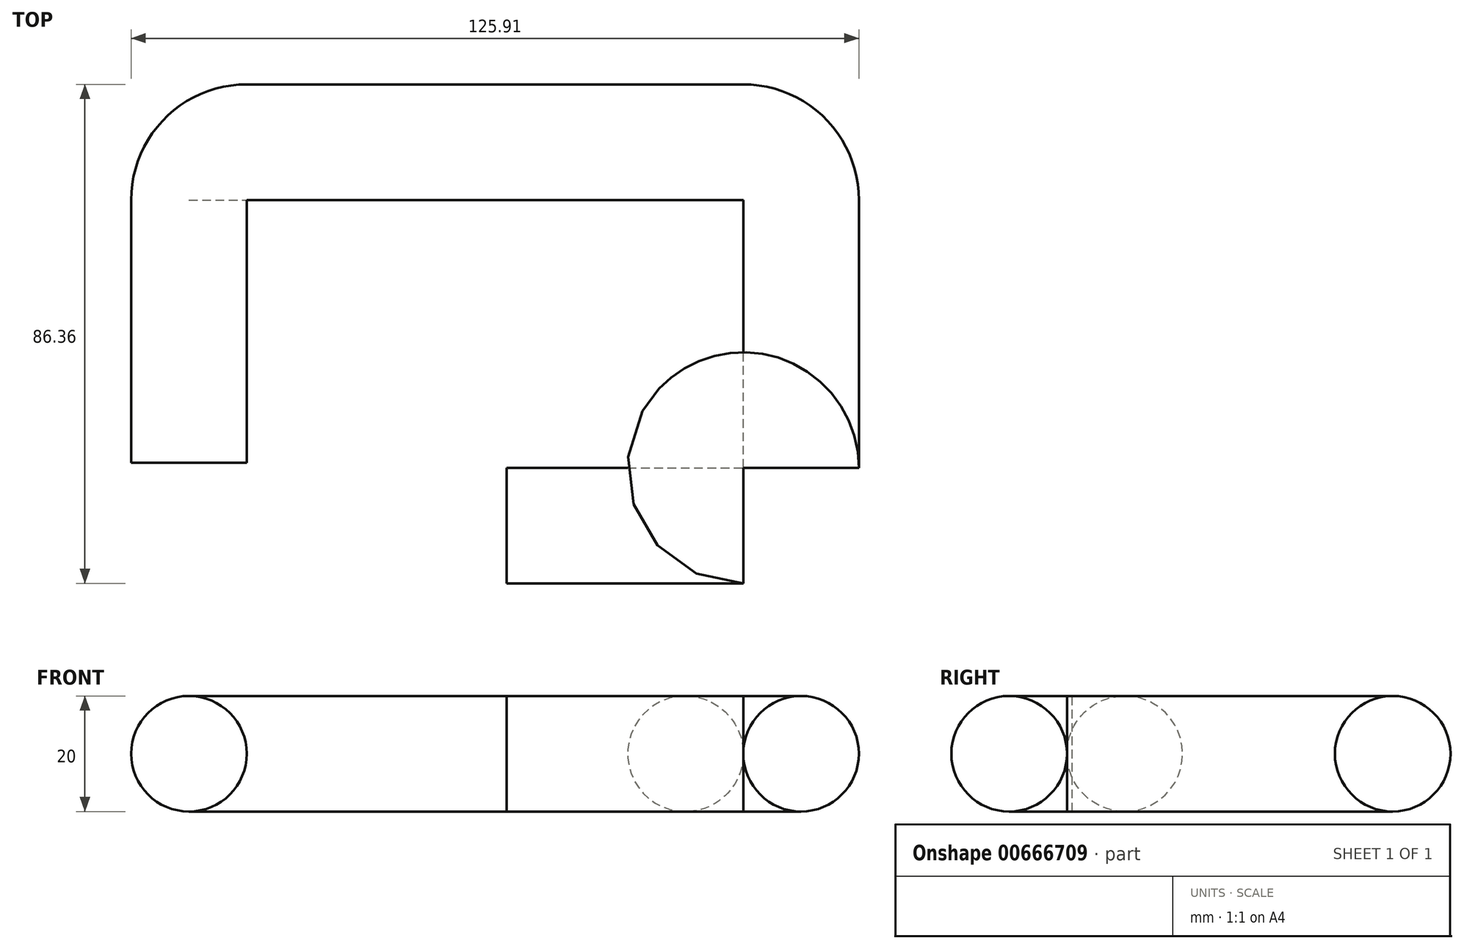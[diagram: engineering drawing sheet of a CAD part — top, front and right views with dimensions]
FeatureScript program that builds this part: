
annotation { "Feature Type Name" : "Feature", "Feature Type Description" : "" }
export const myFeature = defineFeature(function(context is Context, id is Id, definition is map)
    precondition{}
    {
        {
            var Q0;
            Q0=qCreatedBy(makeId("Top.planeOp"),FACE);
            var sketch = newSketch(context, id + "F0", { "sketchPlane" : qUnion([Q0])});
            skLineSegment(sketch, "E0", {"start": v(0, 0) * mm, "end": v(40.96, 0) * mm});
            skLineSegment(sketch, "E1", {"start": v(50.96, 10) * mm, "end": v(50.96, 56.36) * mm});
            skLineSegment(sketch, "E2", {"start": v(-44.95, 66.36) * mm, "end": v(40.96, 66.36) * mm});
            skLineSegment(sketch, "E3", {"start": v(-54.95, 56.36) * mm, "end": v(-54.95, 10.89) * mm});
            skPoint(sketch, "E4.visualSharp", {"position": v(50.96, 66.36) * mm});
            skArc(sketch, "E4.filletArc", {"start": v(50.96, 56.36) * mm, "mid": v(48.03, 63.43) * mm, "end": v(40.96, 66.36) * mm});
            skPoint(sketch, "E5.visualSharp", {"position": v(-54.95, 66.36) * mm});
            skArc(sketch, "E5.filletArc", {"start": v(-44.95, 66.36) * mm, "mid": v(-52.02, 63.43) * mm, "end": v(-54.95, 56.36) * mm});
            skPoint(sketch, "E6.visualSharp", {"position": v(50.96, 0) * mm});
            skArc(sketch, "E6.filletArc", {"start": v(40.96, 0) * mm, "mid": v(48.03, 2.93) * mm, "end": v(50.96, 10) * mm});
            skSolve(sketch);
        }
        {
            var Q0;
            Q0=qCreatedBy(makeId("Right.planeOp"),FACE);
            var sketch = newSketch(context, id + "F1", { "sketchPlane" : qUnion([Q0])});
            skCircle(sketch, "E7", {"center": v(0, 0) * mm, "radius": 10 * mm});
            skSolve(sketch);
        }
        {
            var Q0;
            Q0 = qSketchRegion(id + "F1", true);
            var Q1;
            Q1 = qConstructionFilter(qBodyType(qCreatedBy(id + "F0" ,EDGE), BodyType.WIRE), ConstructionObject.NO);
            sweep(context, id + "F2", {"profiles" : qUnion([Q0]), "path" : qUnion([Q1])});
        }
    });
